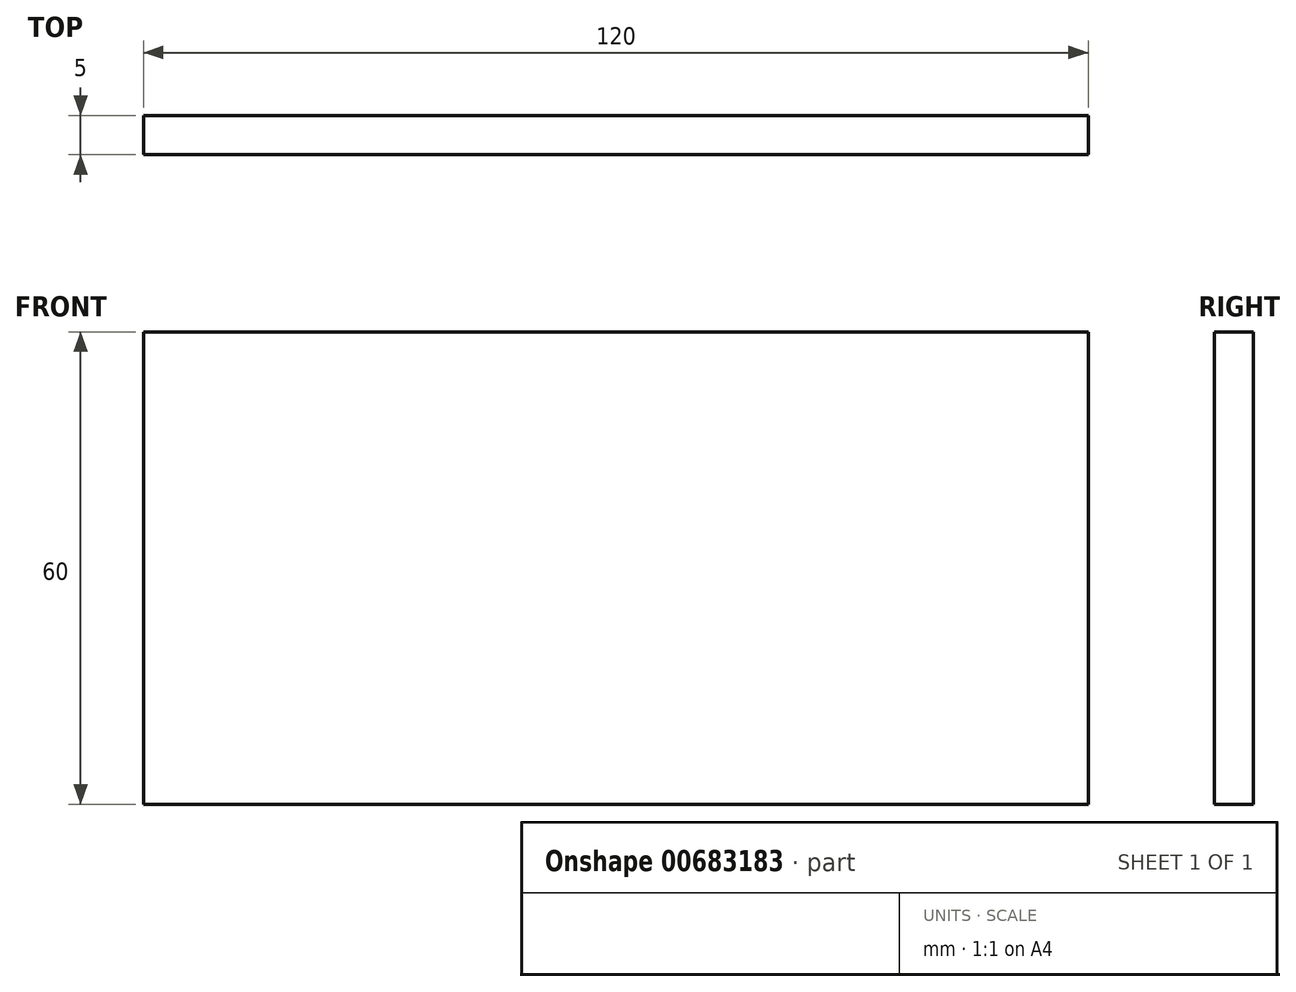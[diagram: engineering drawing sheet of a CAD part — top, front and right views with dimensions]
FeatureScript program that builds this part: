
annotation { "Feature Type Name" : "Feature", "Feature Type Description" : "" }
export const myFeature = defineFeature(function(context is Context, id is Id, definition is map)
    precondition{}
    {
        {
            var Q0;
            Q0=qCreatedBy(makeId("Front.planeOp"),FACE);
            var sketch = newSketch(context, id + "F0", { "sketchPlane" : qUnion([Q0])});
            skLineSegment(sketch, "E0.bottom", {"start": v(60, 30) * mm, "end": v(-60, 30) * mm});
            skLineSegment(sketch, "E0.top", {"start": v(60, -30) * mm, "end": v(-60, -30) * mm});
            skLineSegment(sketch, "E0.left", {"start": v(60, 30) * mm, "end": v(60, -30) * mm});
            skLineSegment(sketch, "E0.right", {"start": v(-60, 30) * mm, "end": v(-60, -30) * mm});
            skPoint(sketch, "E0.middle", {"position": v(0, 0) * mm});
            skSolve(sketch);
        }
        {
            var Q0;
            Q0=makeQuery(id+"F0.imprint","IMPRINT",FACE,{"disambiguationData":[TD([[makeQuery(id+"F0.imprint","IMPRINT",EDGE,{"derivedFrom":sQuery(id+"F0.wireOp",EDGE,"E0.bottom")}),1.0]])]});
            extrude(context, id + "F1", {"entities" : qUnion([Q0]), "depth" : 5 * mm, "offsetDistance" : 25 * mm});
        }
    });
